# Revit family: Furniture_Chairs-Stools-Benches_KUMI_Straw-Chair_EN
name_source: partatom
category: Furniture Systems
revit_build: Autodesk Revit 2018 (Build: 20180329_1100(x64)
units: mm (PartAtom-declared; Revit-internal decimal feet)

## family parameters
Always vertical = No
Cut with Voids When Loaded = No
OmniClass Number = 23.21.23.13.11
OmniClass Title = Residential Chairs
Part Type = Normal
Room Calculation Point = No
Round Connector Dimension = Use Diameter
Shared = No
Work Plane-Based = Yes

## types (2) — shared parameters
Always visible = Yes
BIMobject category = Chairs, Stools & Benches
Description = Straw - a seat-friendly chair with character
Design country = Sweden
Edition number = 1
Frame Material = Kumi - Steel - Black
Frame Material Possibility = Gray or Black
Manufacturer = KUMI
Manufacturer country = Sweden
Manufacturer name = KUMI
Material main = Plywood
Material secondary = Laminate
Product Guid = 8383053e-5cc5-4192-b28e-9e1d87c00278
Product SKU = straw-chair-kumi
Product data url = https://bimobject.com
Product family = Straw
Product group = Chairs
Product name = Straw Chair
Product url = https://www.kumi.se
QR code = https://bimobject.com
Seat Material Possibility = Ash or Black
Seat material = Kumi- Wood - Ash
URL = https://www.kumi.se
zero-valued in all types: Default Elevation

## per-type parameters (varying)
| type | Model |
| Type - (Straw Armchair) | Straw Armchair |
| Type - (Straw Chair) | Straw Chair |

type visibility flags: 2 boolean params named "<type name>" — each type sets only its own to Yes (folded from table)

## geometry (parser evidence)
native form markers: Sweep x2
no freeform markers — native parametric forms only
